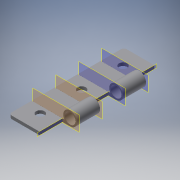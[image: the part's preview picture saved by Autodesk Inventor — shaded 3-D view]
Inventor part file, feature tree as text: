
AUTODESK INVENTOR PART (.ipt)
format: ipt  version: 2019 (Build 230136000, 136)  size: 217,600 bytes
history: native  units: mm
features: other x31, extrude x2, sketch x2, projected_geometry x2, fillet x1
ambient origin geometry x8: Origin, YZ Plane, XZ Plane, XY Plane, X Axis, Y Axis, Z Axis, Center Point
bodies: Body1 (feature_tree), Body2 (feature_tree), Body3 (feature_tree), Body4 (feature_tree)
feature tree (38):
  other  "솔리드1"
  extrude  "돌출1"  Depth=25.0mm
  fillet  "모깎기1"  Radius=2.0mm
  extrude  "돌출2"  Depth=9.0mm
  other  "작업 평면1"
  other  "작업 평면3"
  other  "작업 평면4"
  other  "작업 평면5"
  other  "분할1"
  other  "분할3"
  other  "분할4"
  other  "분할5"
  other  "분할6"
  other  "분할7"
  other  "분할8"
  other  "면 삭제1"
  other  "면 삭제2"
  other  "면 삭제3"
  other  "결합1"
  sketch  "스케치1"
  sketch  "스케치2"
  projected_geometry  "투영된 루프1"
  projected_geometry  "투영된 루프2"
  other  "작업 평면2"
  other  "솔리드2"
  other  "솔리드3"
  other  "솔리드6"
  other  "솔리드7"
  other  "솔리드8"
  other  "솔리드9"
  other  "솔리드10"
  other  "솔리드11"
  other  "솔리드12"
  other  "솔리드13"
  other  "솔리드14"
  other  "솔리드15"
  other  "솔리드16"
  other  "솔리드17"
